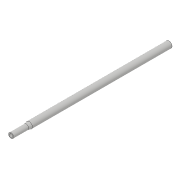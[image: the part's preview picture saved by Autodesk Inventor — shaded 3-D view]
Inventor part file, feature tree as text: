
AUTODESK INVENTOR PART (.ipt)
format: ipt  version: 2018.3 (Build 223284000, 284)  size: 95,744 bytes
history: native  units: in
note: dims shown in document units (in); Inventor stores cm internally (conversion verified against a paired STEP export)
features: sketch x4, extrude x3, revolve x1, projected_geometry x1
ambient origin geometry x8: Origin, YZ Plane, XZ Plane, XY Plane, X Axis, Y Axis, Z Axis, Center Point
bodies: Solid1 (feature_tree)
feature tree (9):
  extrude  "Extrusion1"  Depth=11.125in TaperAngle=0.0deg
  revolve  "Revolution1"  [1 undecoded]
  extrude  "Extrusion2"  TaperAngle=90.0deg  [1 undecoded]
  extrude  "Extrusion3"  Depth=1.44in TaperAngle=0.0deg
  sketch  "Sketch1"  dims[d0=0.51in d1=11.125in d2=0.0in]
  sketch  "Sketch3"  dims[d3=1.44in d4=0.2025in]
  projected_geometry  "Projected Loop1"
  sketch  "Sketch4"  dims[d5=1.2in d6=90.0deg]
  sketch  "Sketch5"  dims[d7=0.291in d8=1.44in d9=0.0in d10=0.406in d11=11.13in d12=0.0in]
note: 2 required parameter values undecoded (feature->parameter linkage not recoverable at this tier; creation-order binding heuristic only, values carry confidence <= 0.55)